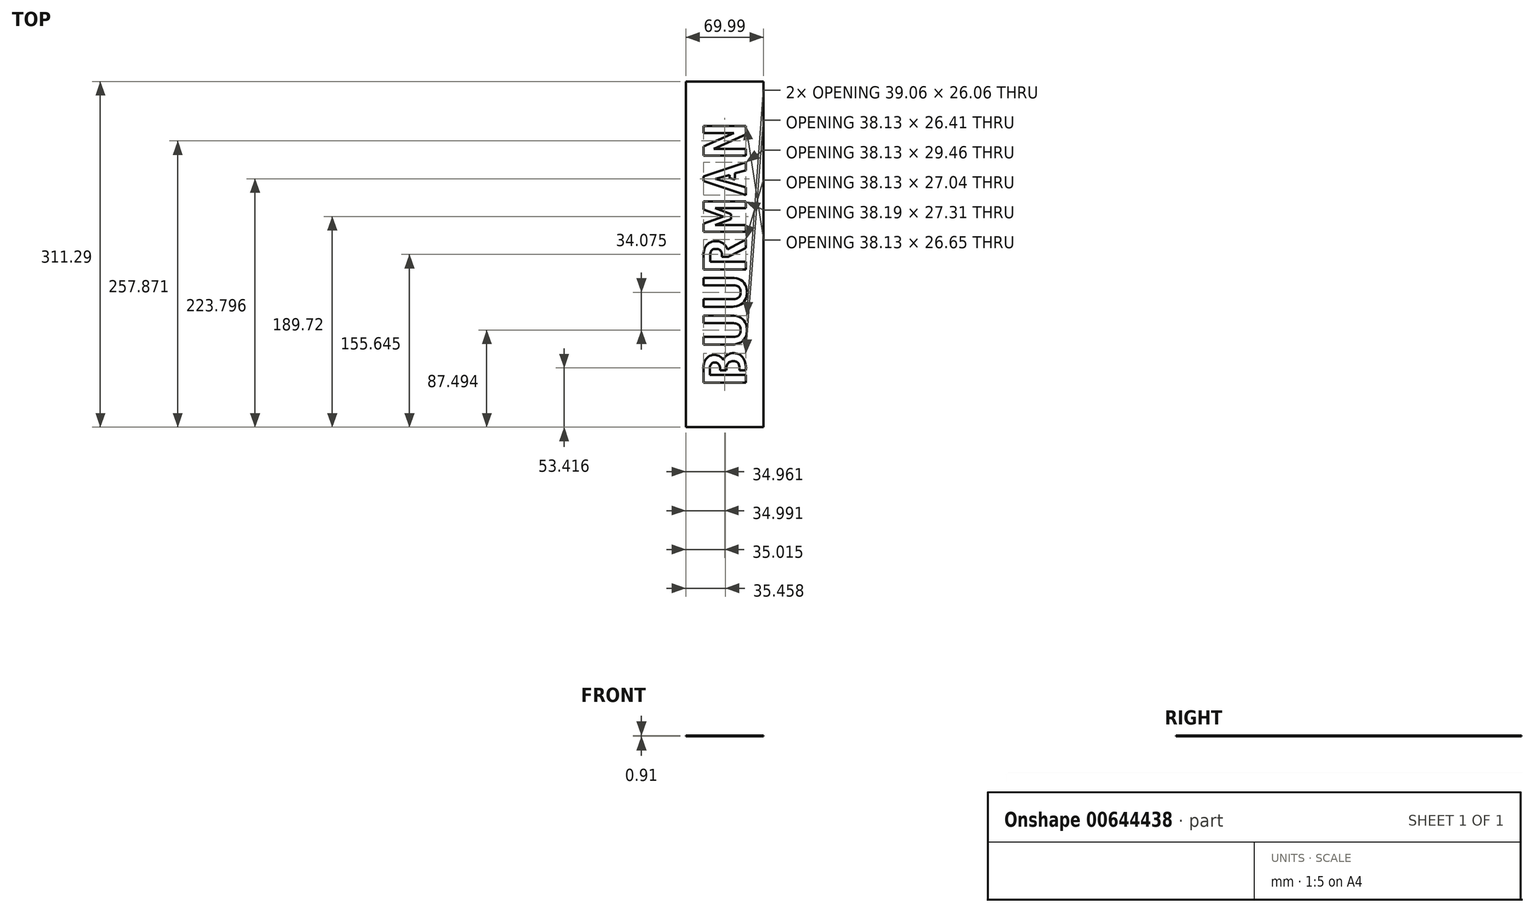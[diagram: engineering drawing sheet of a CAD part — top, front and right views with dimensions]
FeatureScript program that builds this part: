
annotation { "Feature Type Name" : "Feature", "Feature Type Description" : "" }
export const myFeature = defineFeature(function(context is Context, id is Id, definition is map)
    precondition{}
    {
        {
            var Q0;
            Q0=qCreatedBy(makeId("Top.planeOp"),FACE);
            var sketch = newSketch(context, id + "F0", { "sketchPlane" : qUnion([Q0])});
            skLineSegment(sketch, "E0", {"start": v(-753.27, 2930.84) * mm, "end": v(-1506.53, 2930.84) * mm});
            skLineSegment(sketch, "E1", {"start": v(-454.93, 2365.48) * mm, "end": v(-1506.53, 2365.48) * mm});
            skLineSegment(sketch, "E2", {"start": v(-1506.53, 3100.61) * mm, "end": v(-454.93, 3100.61) * mm});
            skLineSegment(sketch, "E3", {"start": v(-1506.53, 2365.48) * mm, "end": v(-1506.53, 2596.24) * mm});
            skLineSegment(sketch, "E4", {"start": v(-454.93, 2535.25) * mm, "end": v(-454.93, 2365.48) * mm});
            skLineSegment(sketch, "E5", {"start": v(-454.93, 2892.1) * mm, "end": v(-1250.22, 2535.25) * mm});
            skLineSegment(sketch, "E6", {"start": v(-1506.53, 2930.84) * mm, "end": v(-1506.53, 3100.61) * mm});
            skLineSegment(sketch, "E7", {"start": v(-454.93, 3100.61) * mm, "end": v(-454.93, 2892.1) * mm});
            skLineSegment(sketch, "E8", {"start": v(-1250.22, 2535.25) * mm, "end": v(-454.93, 2535.25) * mm});
            skLineSegment(sketch, "E9", {"start": v(-1506.53, 2596.24) * mm, "end": v(-753.27, 2930.84) * mm});
            skLineSegment(sketch, "E10", {"start": v(-857.93, 1890.5) * mm, "end": v(-1207.37, 1794.07) * mm});
            skLineSegment(sketch, "E11", {"start": v(-1506.53, 1738.03) * mm, "end": v(-1506.53, 1848.46) * mm});
            skLineSegment(sketch, "E12", {"start": v(-1506.53, 1848.46) * mm, "end": v(-454.93, 2199.55) * mm});
            skLineSegment(sketch, "E13", {"start": v(-454.93, 2199.55) * mm, "end": v(-454.93, 2001.75) * mm});
            skLineSegment(sketch, "E14", {"start": v(-454.93, 1581.44) * mm, "end": v(-454.93, 1386.95) * mm});
            skLineSegment(sketch, "E15", {"start": v(-454.93, 2001.75) * mm, "end": v(-726.9, 1926.76) * mm});
            skLineSegment(sketch, "E16", {"start": v(-726.9, 1926.76) * mm, "end": v(-726.9, 1773.47) * mm});
            skLineSegment(sketch, "E17", {"start": v(-1208.4, 1793.78) * mm, "end": v(-454.93, 1581.44) * mm});
            skLineSegment(sketch, "E18", {"start": v(-454.93, 1386.95) * mm, "end": v(-1506.53, 1738.03) * mm});
            skLineSegment(sketch, "E19", {"start": v(-857.93, 1810.4) * mm, "end": v(-857.93, 1890.5) * mm});
            skLineSegment(sketch, "E20", {"start": v(-1348.44, -2949.46) * mm, "end": v(-1348.44, -3081.32) * mm});
            skLineSegment(sketch, "E21", {"start": v(-1348.44, -3081.32) * mm, "end": v(-454.25, -3081.32) * mm});
            skLineSegment(sketch, "E22", {"start": v(-614.96, -2965.94) * mm, "end": v(-614.96, -2934.62) * mm});
            skLineSegment(sketch, "E23", {"start": v(-454.25, -3081.32) * mm, "end": v(-454.25, -3270.05) * mm});
            skLineSegment(sketch, "E24", {"start": v(-454.25, -3270.05) * mm, "end": v(-1505.85, -3270.05) * mm});
            skLineSegment(sketch, "E25", {"start": v(-1505.85, -3270.05) * mm, "end": v(-1505.85, -2951.1) * mm});
            skLineSegment(sketch, "E26", {"start": v(-829.91, -852.26) * mm, "end": v(-1506.53, -852.26) * mm});
            skLineSegment(sketch, "E27", {"start": v(-1506.53, -852.26) * mm, "end": v(-1506.53, -666.83) * mm});
            skLineSegment(sketch, "E28", {"start": v(-1506.53, -1385.48) * mm, "end": v(-1506.53, -1196.75) * mm});
            skLineSegment(sketch, "E29", {"start": v(-1506.53, -1196.75) * mm, "end": v(-824.97, -1196.75) * mm});
            skLineSegment(sketch, "E30", {"start": v(-826.62, -1385.48) * mm, "end": v(-1506.53, -1385.48) * mm});
            skLineSegment(sketch, "E31", {"start": v(-1506.53, -666.83) * mm, "end": v(-831.56, -666.83) * mm});
            skLineSegment(sketch, "E32", {"start": v(-1506.53, -1606.63) * mm, "end": v(-831.56, -1606.63) * mm});
            skLineSegment(sketch, "E33", {"start": v(-1506.53, -2136.55) * mm, "end": v(-824.97, -2136.55) * mm});
            skLineSegment(sketch, "E34", {"start": v(-826.62, -2325.28) * mm, "end": v(-1506.53, -2325.28) * mm});
            skLineSegment(sketch, "E35", {"start": v(-1506.53, -2325.28) * mm, "end": v(-1506.53, -2136.55) * mm});
            skLineSegment(sketch, "E36", {"start": v(-829.91, -1792.06) * mm, "end": v(-1506.53, -1792.06) * mm});
            skLineSegment(sketch, "E37", {"start": v(-1506.53, -1792.06) * mm, "end": v(-1506.53, -1606.63) * mm});
            skLineSegment(sketch, "E38", {"start": v(-1506.53, 476.81) * mm, "end": v(-1506.53, 676.26) * mm});
            skLineSegment(sketch, "E39", {"start": v(-454.93, 476.81) * mm, "end": v(-1506.53, 476.81) * mm});
            skLineSegment(sketch, "E40", {"start": v(-454.93, 1059.48) * mm, "end": v(-1218.08, 1059.48) * mm});
            skLineSegment(sketch, "E41", {"start": v(-1218.08, 1059.48) * mm, "end": v(-820.85, 912.78) * mm});
            skLineSegment(sketch, "E42", {"start": v(-820.85, 912.78) * mm, "end": v(-820.85, 787.51) * mm});
            skLineSegment(sketch, "E43", {"start": v(-1218.08, 645.76) * mm, "end": v(-454.93, 645.76) * mm});
            skLineSegment(sketch, "E44", {"start": v(-454.93, 645.76) * mm, "end": v(-454.93, 476.81) * mm});
            skLineSegment(sketch, "E45", {"start": v(-820.85, 787.51) * mm, "end": v(-1218.08, 645.76) * mm});
            skLineSegment(sketch, "E46", {"start": v(-1506.53, 676.26) * mm, "end": v(-1012.05, 853.45) * mm});
            skLineSegment(sketch, "E47", {"start": v(-1012.05, 853.45) * mm, "end": v(-1508.18, 1028.99) * mm});
            skLineSegment(sketch, "E48", {"start": v(-1508.18, 1028.99) * mm, "end": v(-1508.18, 1230.08) * mm});
            skLineSegment(sketch, "E49", {"start": v(-1508.18, 1230.08) * mm, "end": v(-454.93, 1230.08) * mm});
            skLineSegment(sketch, "E50", {"start": v(-454.93, 1230.08) * mm, "end": v(-454.93, 1059.48) * mm});
            skLineSegment(sketch, "E51", {"start": v(-1506.53, -459.28) * mm, "end": v(-1506.53, -126.32) * mm});
            skLineSegment(sketch, "E52", {"start": v(-454.93, 286.57) * mm, "end": v(-454.93, 73.94) * mm});
            skLineSegment(sketch, "E53", {"start": v(-912.33, 40.15) * mm, "end": v(-454.93, 286.57) * mm});
            skLineSegment(sketch, "E54", {"start": v(-454.93, 73.94) * mm, "end": v(-890.07, -143.63) * mm});
            skLineSegment(sketch, "E55", {"start": v(-1339.23, -266.43) * mm, "end": v(-454.93, -266.43) * mm});
            skLineSegment(sketch, "E56", {"start": v(-454.93, -266.43) * mm, "end": v(-454.93, -459.28) * mm});
            skLineSegment(sketch, "E57", {"start": v(-1050.78, -143.63) * mm, "end": v(-1050.78, -114.79) * mm});
            skLineSegment(sketch, "E58", {"start": v(-1339.23, -114.79) * mm, "end": v(-1339.23, -266.43) * mm});
            skLineSegment(sketch, "E59", {"start": v(-454.93, -459.28) * mm, "end": v(-1506.53, -459.28) * mm});
            skFitSpline(sketch, "E60", {"points": [v(-1505.85, -2951.1) * mm, v(-1503.48, -2896.62) * mm, v(-1500.12, -2819.58) * mm, v(-1467.8, -2727.6) * mm, v(-1435.59, -2674.72) * mm, v(-1395, -2633.67) * mm, v(-1347.26, -2604.12) * mm, v(-1292.6, -2587) * mm, v(-1232.83, -2581.22) * mm, v(-1169.39, -2589.48) * mm, v(-1109, -2616.14) * mm, v(-1054.43, -2655.71) * mm, v(-1030.03, -2692.88) * mm, v(-1017.96, -2711.28) * mm]});
            skFitSpline(sketch, "E61", {"points": [v(-1017.96, -2711.28) * mm, v(-998.63, -2680.55) * mm, v(-959.8, -2618.83) * mm, v(-867.71, -2559.04) * mm, v(-774.7, -2538.13) * mm, v(-696.27, -2546.32) * mm, v(-634, -2565.32) * mm, v(-579.68, -2598.47) * mm, v(-533.73, -2644.51) * mm, v(-497.24, -2703.7) * mm, v(-471.97, -2775.8) * mm, v(-455.93, -2864.54) * mm, v(-454.86, -2929.39) * mm, v(-454.25, -2965.94) * mm]});
            skFitSpline(sketch, "E62", {"points": [v(-942.14, -2965.94) * mm, v(-940.98, -2930.74) * mm, v(-938.96, -2869.63) * mm, v(-901.55, -2791.6) * mm, v(-840, -2747.52) * mm, v(-768.48, -2736.85) * mm, v(-698.63, -2745.12) * mm, v(-643.77, -2788.35) * mm, v(-618.55, -2856.44) * mm, v(-616.24, -2906.61) * mm, v(-614.96, -2934.62) * mm]});
            skFitSpline(sketch, "E63", {"points": [v(-1348.44, -2949.46) * mm, v(-1346.26, -2916.2) * mm, v(-1342.43, -2857.88) * mm, v(-1293.4, -2788.35) * mm, v(-1227.62, -2769) * mm, v(-1169.26, -2780.88) * mm, v(-1123.55, -2819.55) * mm, v(-1098.16, -2885.62) * mm, v(-1096.43, -2936.6) * mm, v(-1095.43, -2965.94) * mm]});
            skFitSpline(sketch, "E64", {"points": [v(-824.97, -2136.55) * mm, v(-790.76, -2135.1) * mm, v(-730.02, -2132.55) * mm, v(-648.06, -2105.71) * mm, v(-594.62, -2044.75) * mm, v(-585.1, -1965.28) * mm, v(-594.6, -1885.44) * mm, v(-648.85, -1823.05) * mm, v(-732.73, -1796.08) * mm, v(-794.83, -1793.51) * mm, v(-829.91, -1792.06) * mm]});
            skFitSpline(sketch, "E65", {"points": [v(-826.62, -2325.28) * mm, v(-797.07, -2324.3) * mm, v(-740.86, -2322.45) * mm, v(-661.6, -2305.13) * mm, v(-592.4, -2276.43) * mm, v(-533.9, -2235.75) * mm, v(-487.12, -2183.7) * mm, v(-453.97, -2120.47) * mm, v(-434.69, -2047.19) * mm, v(-429.13, -1968.13) * mm, v(-434.61, -1889.34) * mm, v(-453.25, -1816.8) * mm, v(-485.22, -1753.44) * mm, v(-530.1, -1699.8) * mm, v(-588, -1657.08) * mm, v(-658.7, -1627.37) * mm, v(-741.26, -1609.5) * mm, v(-800.28, -1607.62) * mm, v(-831.56, -1606.63) * mm]});
            skFitSpline(sketch, "E66", {"points": [v(-824.97, -1196.75) * mm, v(-790.76, -1195.3) * mm, v(-730.02, -1192.75) * mm, v(-648.06, -1165.91) * mm, v(-594.62, -1104.95) * mm, v(-585.1, -1025.48) * mm, v(-594.6, -945.64) * mm, v(-648.85, -883.25) * mm, v(-732.73, -856.28) * mm, v(-794.83, -853.71) * mm, v(-829.91, -852.26) * mm]});
            skFitSpline(sketch, "E67", {"points": [v(-826.62, -1385.48) * mm, v(-797.07, -1384.5) * mm, v(-740.86, -1382.65) * mm, v(-661.6, -1365.33) * mm, v(-592.4, -1336.63) * mm, v(-533.9, -1295.95) * mm, v(-487.12, -1243.9) * mm, v(-453.97, -1180.67) * mm, v(-434.69, -1107.39) * mm, v(-429.13, -1028.33) * mm, v(-434.61, -949.54) * mm, v(-453.25, -877) * mm, v(-485.22, -813.64) * mm, v(-530.1, -760) * mm, v(-588, -717.28) * mm, v(-658.7, -687.57) * mm, v(-741.26, -669.7) * mm, v(-800.28, -667.82) * mm, v(-831.56, -666.83) * mm]});
            skFitSpline(sketch, "E68", {"points": [v(-1339.23, -114.79) * mm, v(-1338.12, -90.2) * mm, v(-1336.13, -46.45) * mm, v(-1307.65, 11.42) * mm, v(-1254.87, 43.27) * mm, v(-1194.45, 50.15) * mm, v(-1134, 42.36) * mm, v(-1084.26, 9.43) * mm, v(-1054.21, -46.95) * mm, v(-1052, -90.63) * mm, v(-1050.78, -114.79) * mm]});
            skFitSpline(sketch, "E69", {"points": [v(-1506.53, -126.32) * mm, v(-1505.68, -96.86) * mm, v(-1504.1, -41.6) * mm, v(-1488.74, 35.3) * mm, v(-1463.23, 100.39) * mm, v(-1426.14, 152.94) * mm, v(-1379.35, 192.97) * mm, v(-1324.2, 221.52) * mm, v(-1260.88, 237.89) * mm, v(-1196.63, 243.26) * mm, v(-1133.5, 236.96) * mm, v(-1075.94, 217.61) * mm, v(-1021.55, 187.5) * mm, v(-974.14, 146.75) * mm, v(-934.94, 97.76) * mm, v(-919.84, 59.29) * mm, v(-912.33, 40.15) * mm]});
            skLineSegment(sketch, "E70", {"start": v(-1095.43, -2965.94) * mm, "end": v(-942.14, -2965.94) * mm});
            skLineSegment(sketch, "E71", {"start": v(-614.96, -2965.94) * mm, "end": v(-454.25, -2965.94) * mm});
            skLineSegment(sketch, "E72", {"start": v(-1050.78, -143.63) * mm, "end": v(-890.07, -143.63) * mm});
            skLineSegment(sketch, "E73", {"start": v(-726.9, 1773.47) * mm, "end": v(-857.93, 1810.4) * mm});
            skLineSegment(sketch, "E74", {"start": v(-15.5, -4378.95) * mm, "end": v(-1945.9, -4378.95) * mm});
            skLineSegment(sketch, "E75", {"start": v(-15.5, 4206.25) * mm, "end": v(-1945.9, 4206.25) * mm});
            skLineSegment(sketch, "E76", {"start": v(-15.5, -4378.95) * mm, "end": v(-15.5, 4206.25) * mm});
            skLineSegment(sketch, "E77", {"start": v(-1945.9, 4206.25) * mm, "end": v(-1945.9, -4378.95) * mm});
            skLineSegment(sketch, "E78", {"start": v(-1506.53, 1738.03) * mm, "end": v(-454.93, 1386.95) * mm});
            skLineSegment(sketch, "E79", {"start": v(-454.93, 1386.95) * mm, "end": v(-454.93, 1581.44) * mm});
            skLineSegment(sketch, "E80", {"start": v(-454.93, 1581.44) * mm, "end": v(-1207.37, 1794.07) * mm});
            skLineSegment(sketch, "E81", {"start": v(-1207.37, 1794.07) * mm, "end": v(-857.93, 1890.5) * mm});
            skLineSegment(sketch, "E82", {"start": v(-857.93, 1890.5) * mm, "end": v(-857.93, 1810.4) * mm});
            skLineSegment(sketch, "E83", {"start": v(-857.93, 1810.4) * mm, "end": v(-726.9, 1773.47) * mm});
            skLineSegment(sketch, "E84", {"start": v(-726.9, 1773.47) * mm, "end": v(-726.9, 1926.76) * mm});
            skLineSegment(sketch, "E85", {"start": v(-726.9, 1926.76) * mm, "end": v(-454.93, 2001.75) * mm});
            skLineSegment(sketch, "E86", {"start": v(-454.93, 2001.75) * mm, "end": v(-454.93, 2199.55) * mm});
            skLineSegment(sketch, "E87", {"start": v(-454.93, 2199.55) * mm, "end": v(-1506.53, 1848.46) * mm});
            skLineSegment(sketch, "E88", {"start": v(-1506.53, 1848.46) * mm, "end": v(-1506.53, 1738.03) * mm});
            skSolve(sketch);
        }
        {
            var Q0;
            Q0 = qSketchRegion(id + "F0", true);
            extrude(context, id + "F1", {"entities" : qUnion([Q0]), "depth" : 25 * mm, "offsetDistance" : 25 * mm});
        }
        {
            var Q0;
            Q0=makeQuery(id+"F1.opExtrude","SWEPT_BODY",BODY,{"disambiguationData":[OSD([sQuery(id+"F0.wireOp",EDGE,"E0"),sQuery(id+"F0.wireOp",EDGE,"E1"),sQuery(id+"F0.wireOp",EDGE,"E2"),sQuery(id+"F0.wireOp",EDGE,"E3"),sQuery(id+"F0.wireOp",EDGE,"E4"),sQuery(id+"F0.wireOp",EDGE,"E5"),sQuery(id+"F0.wireOp",EDGE,"E6"),sQuery(id+"F0.wireOp",EDGE,"E7"),sQuery(id+"F0.wireOp",EDGE,"E8"),sQuery(id+"F0.wireOp",EDGE,"E9"),sQuery(id+"F0.wireOp",EDGE,"E20"),sQuery(id+"F0.wireOp",EDGE,"E21"),sQuery(id+"F0.wireOp",EDGE,"E22"),sQuery(id+"F0.wireOp",EDGE,"E23"),sQuery(id+"F0.wireOp",EDGE,"E24"),sQuery(id+"F0.wireOp",EDGE,"E25"),sQuery(id+"F0.wireOp",EDGE,"E26"),sQuery(id+"F0.wireOp",EDGE,"E27"),sQuery(id+"F0.wireOp",EDGE,"E28"),sQuery(id+"F0.wireOp",EDGE,"E29"),sQuery(id+"F0.wireOp",EDGE,"E30"),sQuery(id+"F0.wireOp",EDGE,"E31"),sQuery(id+"F0.wireOp",EDGE,"E32"),sQuery(id+"F0.wireOp",EDGE,"E33"),sQuery(id+"F0.wireOp",EDGE,"E34"),sQuery(id+"F0.wireOp",EDGE,"E35"),sQuery(id+"F0.wireOp",EDGE,"E36"),sQuery(id+"F0.wireOp",EDGE,"E37"),sQuery(id+"F0.wireOp",EDGE,"E38"),sQuery(id+"F0.wireOp",EDGE,"E39"),sQuery(id+"F0.wireOp",EDGE,"E40"),sQuery(id+"F0.wireOp",EDGE,"E41"),sQuery(id+"F0.wireOp",EDGE,"E42"),sQuery(id+"F0.wireOp",EDGE,"E43"),sQuery(id+"F0.wireOp",EDGE,"E44"),sQuery(id+"F0.wireOp",EDGE,"E45"),sQuery(id+"F0.wireOp",EDGE,"E46"),sQuery(id+"F0.wireOp",EDGE,"E47"),sQuery(id+"F0.wireOp",EDGE,"E48"),sQuery(id+"F0.wireOp",EDGE,"E49"),sQuery(id+"F0.wireOp",EDGE,"E50"),sQuery(id+"F0.wireOp",EDGE,"E51"),sQuery(id+"F0.wireOp",EDGE,"E52"),sQuery(id+"F0.wireOp",EDGE,"E53"),sQuery(id+"F0.wireOp",EDGE,"E54"),sQuery(id+"F0.wireOp",EDGE,"E55"),sQuery(id+"F0.wireOp",EDGE,"E56"),sQuery(id+"F0.wireOp",EDGE,"E57"),sQuery(id+"F0.wireOp",EDGE,"E58"),sQuery(id+"F0.wireOp",EDGE,"E59"),sQuery(id+"F0.wireOp",EDGE,"E60"),sQuery(id+"F0.wireOp",EDGE,"E61"),sQuery(id+"F0.wireOp",EDGE,"E62"),sQuery(id+"F0.wireOp",EDGE,"E63"),sQuery(id+"F0.wireOp",EDGE,"E64"),sQuery(id+"F0.wireOp",EDGE,"E65"),sQuery(id+"F0.wireOp",EDGE,"E66"),sQuery(id+"F0.wireOp",EDGE,"E67"),sQuery(id+"F0.wireOp",EDGE,"E68"),sQuery(id+"F0.wireOp",EDGE,"E69"),sQuery(id+"F0.wireOp",EDGE,"E70"),sQuery(id+"F0.wireOp",EDGE,"E71"),sQuery(id+"F0.wireOp",EDGE,"E72"),sQuery(id+"F0.wireOp",EDGE,"E74"),sQuery(id+"F0.wireOp",EDGE,"E75"),sQuery(id+"F0.wireOp",EDGE,"E76"),sQuery(id+"F0.wireOp",EDGE,"E77"),sQuery(id+"F0.wireOp",EDGE,"E78"),sQuery(id+"F0.wireOp",EDGE,"E79"),sQuery(id+"F0.wireOp",EDGE,"E80"),sQuery(id+"F0.wireOp",EDGE,"E81"),sQuery(id+"F0.wireOp",EDGE,"E82"),sQuery(id+"F0.wireOp",EDGE,"E83"),sQuery(id+"F0.wireOp",EDGE,"E84"),sQuery(id+"F0.wireOp",EDGE,"E85"),sQuery(id+"F0.wireOp",EDGE,"E86"),sQuery(id+"F0.wireOp",EDGE,"E87"),sQuery(id+"F0.wireOp",EDGE,"E88")])]});
            var Q1;
            Q1=makeQuery(id+"F1.opExtrude","CAP_VERTEX",VERTEX,{"disambiguationData":[OSD([sQuery(id+"F0.wireOp",EDGE,"E23"),sQuery(id+"F0.wireOp",EDGE,"E24")])],"isStart":false});
            transform(context, id + "F2", {"entities" : qUnion([Q0]), "transformType" : TransformType.SCALE_UNIFORMLY, "scale" : 1 / 27.58, "scalePoint" : qUnion([Q1]), "makeCopy" : false});
        }
        {
            var Q0;
            Q0=qCreatedBy(makeId("Top.planeOp"),FACE);
            var sketch = newSketch(context, id + "F3", { "sketchPlane" : qUnion([Q0])});
            skLineSegment(sketch, "E89", {"start": v(-128.42, 679.2) * mm, "end": v(-128.42, 1568.2) * mm});
            skLineSegment(sketch, "E90", {"start": v(-128.42, 1568.2) * mm, "end": v(-382.42, 1568.2) * mm});
            skLineSegment(sketch, "E91", {"start": v(-382.42, 1568.2) * mm, "end": v(-382.42, 1644.4) * mm});
            skLineSegment(sketch, "E92", {"start": v(-382.42, 1644.4) * mm, "end": v(-890.42, 1644.4) * mm});
            skLineSegment(sketch, "E93", {"start": v(-890.42, 1644.4) * mm, "end": v(-890.42, 1568.2) * mm});
            skLineSegment(sketch, "E94", {"start": v(-890.42, 1568.2) * mm, "end": v(-1144.42, 1568.2) * mm});
            skLineSegment(sketch, "E95", {"start": v(-1144.42, 1568.2) * mm, "end": v(-1144.42, 679.2) * mm});
            skLineSegment(sketch, "E96", {"start": v(-1144.42, -5975.6) * mm, "end": v(-890.42, -5975.6) * mm});
            skLineSegment(sketch, "E97", {"start": v(-890.42, -5975.6) * mm, "end": v(-890.42, -5899.4) * mm});
            skLineSegment(sketch, "E98", {"start": v(-890.42, -5899.4) * mm, "end": v(-1144.42, -5899.4) * mm});
            skLineSegment(sketch, "E99", {"start": v(-1144.42, -5899.4) * mm, "end": v(-1144.42, -5035.8) * mm});
            skLineSegment(sketch, "E100", {"start": v(-128.42, -5975.6) * mm, "end": v(-382.42, -5975.6) * mm});
            skLineSegment(sketch, "E101", {"start": v(-382.42, -5975.6) * mm, "end": v(-382.42, -5899.4) * mm});
            skLineSegment(sketch, "E102", {"start": v(-382.42, -5899.4) * mm, "end": v(-128.42, -5899.4) * mm});
            skLineSegment(sketch, "E103", {"start": v(-128.42, -5899.4) * mm, "end": v(-128.42, -5035.8) * mm});
            skLineSegment(sketch, "E104", {"start": v(-1144.42, -5035.8) * mm, "end": v(-890.42, -5035.8) * mm});
            skLineSegment(sketch, "E105", {"start": v(-890.42, -5035.8) * mm, "end": v(-890.42, -4959.6) * mm});
            skLineSegment(sketch, "E106", {"start": v(-890.42, -4959.6) * mm, "end": v(-1144.42, -4959.6) * mm});
            skLineSegment(sketch, "E107", {"start": v(-1144.42, -4959.6) * mm, "end": v(-1144.42, -4096) * mm});
            skLineSegment(sketch, "E108", {"start": v(-128.42, -5035.8) * mm, "end": v(-382.42, -5035.8) * mm});
            skLineSegment(sketch, "E109", {"start": v(-382.42, -5035.8) * mm, "end": v(-382.42, -4959.6) * mm});
            skLineSegment(sketch, "E110", {"start": v(-382.42, -4959.6) * mm, "end": v(-128.42, -4959.6) * mm});
            skLineSegment(sketch, "E111", {"start": v(-128.42, -4959.6) * mm, "end": v(-128.42, -4096) * mm});
            skLineSegment(sketch, "E112", {"start": v(-1144.42, -4096) * mm, "end": v(-890.42, -4096) * mm});
            skLineSegment(sketch, "E113", {"start": v(-890.42, -4096) * mm, "end": v(-890.42, -4019.8) * mm});
            skLineSegment(sketch, "E114", {"start": v(-890.42, -4019.8) * mm, "end": v(-1144.42, -4019.8) * mm});
            skLineSegment(sketch, "E115", {"start": v(-1144.42, -4019.8) * mm, "end": v(-1144.42, -3156.2) * mm});
            skLineSegment(sketch, "E116", {"start": v(-128.42, -4096) * mm, "end": v(-382.42, -4096) * mm});
            skLineSegment(sketch, "E117", {"start": v(-382.42, -4096) * mm, "end": v(-382.42, -4019.8) * mm});
            skLineSegment(sketch, "E118", {"start": v(-382.42, -4019.8) * mm, "end": v(-128.42, -4019.8) * mm});
            skLineSegment(sketch, "E119", {"start": v(-128.42, -4019.8) * mm, "end": v(-128.42, -3156.2) * mm});
            skLineSegment(sketch, "E120", {"start": v(-1144.42, -3156.2) * mm, "end": v(-890.42, -3156.2) * mm});
            skLineSegment(sketch, "E121", {"start": v(-890.42, -3156.2) * mm, "end": v(-890.42, -3080) * mm});
            skLineSegment(sketch, "E122", {"start": v(-890.42, -3080) * mm, "end": v(-1144.42, -3080) * mm});
            skLineSegment(sketch, "E123", {"start": v(-1144.42, -3080) * mm, "end": v(-1144.42, -2216.4) * mm});
            skLineSegment(sketch, "E124", {"start": v(-128.42, -3156.2) * mm, "end": v(-382.42, -3156.2) * mm});
            skLineSegment(sketch, "E125", {"start": v(-382.42, -3156.2) * mm, "end": v(-382.42, -3080) * mm});
            skLineSegment(sketch, "E126", {"start": v(-382.42, -3080) * mm, "end": v(-128.42, -3080) * mm});
            skLineSegment(sketch, "E127", {"start": v(-128.42, -3080) * mm, "end": v(-128.42, -2216.4) * mm});
            skLineSegment(sketch, "E128", {"start": v(-1144.42, -2216.4) * mm, "end": v(-890.42, -2216.4) * mm});
            skLineSegment(sketch, "E129", {"start": v(-890.42, -2216.4) * mm, "end": v(-890.42, -2140.2) * mm});
            skLineSegment(sketch, "E130", {"start": v(-890.42, -2140.2) * mm, "end": v(-1144.42, -2140.2) * mm});
            skLineSegment(sketch, "E131", {"start": v(-1144.42, -2140.2) * mm, "end": v(-1144.42, -1276.6) * mm});
            skLineSegment(sketch, "E132", {"start": v(-128.42, -2216.4) * mm, "end": v(-382.42, -2216.4) * mm});
            skLineSegment(sketch, "E133", {"start": v(-382.42, -2216.4) * mm, "end": v(-382.42, -2140.2) * mm});
            skLineSegment(sketch, "E134", {"start": v(-382.42, -2140.2) * mm, "end": v(-128.42, -2140.2) * mm});
            skLineSegment(sketch, "E135", {"start": v(-128.42, -2140.2) * mm, "end": v(-128.42, -1276.6) * mm});
            skLineSegment(sketch, "E136", {"start": v(-1144.42, -1276.6) * mm, "end": v(-890.42, -1276.6) * mm});
            skLineSegment(sketch, "E137", {"start": v(-890.42, -1276.6) * mm, "end": v(-890.42, -1200.4) * mm});
            skLineSegment(sketch, "E138", {"start": v(-890.42, -1200.4) * mm, "end": v(-1144.42, -1200.4) * mm});
            skLineSegment(sketch, "E139", {"start": v(-1144.42, -1200.4) * mm, "end": v(-1144.42, -336.8) * mm});
            skLineSegment(sketch, "E140", {"start": v(-128.42, -1276.6) * mm, "end": v(-382.42, -1276.6) * mm});
            skLineSegment(sketch, "E141", {"start": v(-382.42, -1276.6) * mm, "end": v(-382.42, -1200.4) * mm});
            skLineSegment(sketch, "E142", {"start": v(-382.42, -1200.4) * mm, "end": v(-128.42, -1200.4) * mm});
            skLineSegment(sketch, "E143", {"start": v(-128.42, -1200.4) * mm, "end": v(-128.42, -336.8) * mm});
            skLineSegment(sketch, "E144", {"start": v(-1144.42, -336.8) * mm, "end": v(-890.42, -336.8) * mm});
            skLineSegment(sketch, "E145", {"start": v(-890.42, -336.8) * mm, "end": v(-890.42, -260.6) * mm});
            skLineSegment(sketch, "E146", {"start": v(-890.42, -260.6) * mm, "end": v(-1144.42, -260.6) * mm});
            skLineSegment(sketch, "E147", {"start": v(-1144.42, -260.6) * mm, "end": v(-1144.42, 603) * mm});
            skLineSegment(sketch, "E148", {"start": v(-128.42, -336.8) * mm, "end": v(-382.42, -336.8) * mm});
            skLineSegment(sketch, "E149", {"start": v(-382.42, -336.8) * mm, "end": v(-382.42, -260.6) * mm});
            skLineSegment(sketch, "E150", {"start": v(-382.42, -260.6) * mm, "end": v(-128.42, -260.6) * mm});
            skLineSegment(sketch, "E151", {"start": v(-128.42, -260.6) * mm, "end": v(-128.42, 603) * mm});
            skLineSegment(sketch, "E152", {"start": v(-1144.42, 603) * mm, "end": v(-890.42, 603) * mm});
            skLineSegment(sketch, "E153", {"start": v(-890.42, 603) * mm, "end": v(-890.42, 679.2) * mm});
            skLineSegment(sketch, "E154", {"start": v(-890.42, 679.2) * mm, "end": v(-1144.42, 679.2) * mm});
            skLineSegment(sketch, "E155", {"start": v(-128.42, 603) * mm, "end": v(-382.42, 603) * mm});
            skLineSegment(sketch, "E156", {"start": v(-382.42, 603) * mm, "end": v(-382.42, 679.2) * mm});
            skLineSegment(sketch, "E157", {"start": v(-382.42, 679.2) * mm, "end": v(-128.42, 679.2) * mm});
            skLineSegment(sketch, "E158", {"start": v(-1144.42, -5975.6) * mm, "end": v(-1144.42, -6864.6) * mm});
            skLineSegment(sketch, "E159", {"start": v(-1144.42, -6864.6) * mm, "end": v(-890.42, -6864.6) * mm});
            skLineSegment(sketch, "E160", {"start": v(-890.42, -6864.6) * mm, "end": v(-890.42, -6940.8) * mm});
            skLineSegment(sketch, "E161", {"start": v(-890.42, -6940.8) * mm, "end": v(-382.42, -6940.8) * mm});
            skLineSegment(sketch, "E162", {"start": v(-382.42, -6940.8) * mm, "end": v(-382.42, -6864.6) * mm});
            skLineSegment(sketch, "E163", {"start": v(-382.42, -6864.6) * mm, "end": v(-128.42, -6864.6) * mm});
            skLineSegment(sketch, "E164", {"start": v(-128.42, -6864.6) * mm, "end": v(-128.42, -5975.6) * mm});
            skSolve(sketch);
        }
        {
            var Q0;
            Q0=sQuery(id+"F3.wireOp",EDGE,"E161");
            var Q1;
            Q1=sQuery(id+"F3.wireOp",EDGE,"E158");
            var Q2;
            Q2=sQuery(id+"F3.wireOp",EDGE,"E151");
            var Q3;
            Q3=sQuery(id+"F3.wireOp",EDGE,"E119");
            var Q4;
            Q4=sQuery(id+"F3.wireOp",EDGE,"E135");
            var Q5;
            Q5=sQuery(id+"F3.wireOp",EDGE,"E111");
            var Q6;
            Q6=sQuery(id+"F3.wireOp",EDGE,"E143");
            var Q7;
            Q7=sQuery(id+"F3.wireOp",EDGE,"E127");
            var Q8;
            Q8=sQuery(id+"F3.wireOp",EDGE,"E103");
            var Q9;
            Q9=sQuery(id+"F3.wireOp",EDGE,"E107");
            var Q10;
            Q10=sQuery(id+"F3.wireOp",EDGE,"E139");
            var Q11;
            Q11=sQuery(id+"F3.wireOp",EDGE,"E123");
            var Q12;
            Q12=sQuery(id+"F3.wireOp",EDGE,"E89");
            var Q13;
            Q13=sQuery(id+"F3.wireOp",EDGE,"E92");
            var Q14;
            Q14=sQuery(id+"F3.wireOp",EDGE,"E95");
            var Q15;
            Q15=sQuery(id+"F3.wireOp",EDGE,"E99");
            var Q16;
            Q16=sQuery(id+"F3.wireOp",EDGE,"E115");
            var Q17;
            Q17=sQuery(id+"F3.wireOp",EDGE,"E131");
            var Q18;
            Q18=sQuery(id+"F3.wireOp",EDGE,"E147");
            var Q19;
            Q19=sQuery(id+"F3.wireOp",EDGE,"E164");
            var Q20;
            Q20=sQuery(id+"F3.wireOp",EDGE,"E160");
            var Q21;
            Q21=sQuery(id+"F3.wireOp",EDGE,"E149");
            var Q22;
            Q22=sQuery(id+"F3.wireOp",EDGE,"E133");
            var Q23;
            Q23=sQuery(id+"F3.wireOp",EDGE,"E117");
            var Q24;
            Q24=sQuery(id+"F3.wireOp",EDGE,"E145");
            var Q25;
            Q25=sQuery(id+"F3.wireOp",EDGE,"E129");
            var Q26;
            Q26=sQuery(id+"F3.wireOp",EDGE,"E113");
            var Q27;
            Q27=sQuery(id+"F3.wireOp",EDGE,"E110");
            var Q28;
            Q28=sQuery(id+"F3.wireOp",EDGE,"E142");
            var Q29;
            Q29=sQuery(id+"F3.wireOp",EDGE,"E126");
            var Q30;
            Q30=sQuery(id+"F3.wireOp",EDGE,"E106");
            var Q31;
            Q31=sQuery(id+"F3.wireOp",EDGE,"E154");
            var Q32;
            Q32=sQuery(id+"F3.wireOp",EDGE,"E138");
            var Q33;
            Q33=sQuery(id+"F3.wireOp",EDGE,"E122");
            var Q34;
            Q34=sQuery(id+"F3.wireOp",EDGE,"E130");
            var Q35;
            Q35=sQuery(id+"F3.wireOp",EDGE,"E146");
            var Q36;
            Q36=sQuery(id+"F3.wireOp",EDGE,"E114");
            var Q37;
            Q37=sQuery(id+"F3.wireOp",EDGE,"E162");
            var Q38;
            Q38=sQuery(id+"F3.wireOp",EDGE,"E152");
            var Q39;
            Q39=sQuery(id+"F3.wireOp",EDGE,"E159");
            var Q40;
            Q40=sQuery(id+"F3.wireOp",EDGE,"E136");
            var Q41;
            Q41=sQuery(id+"F3.wireOp",EDGE,"E120");
            var Q42;
            Q42=sQuery(id+"F3.wireOp",EDGE,"E102");
            var Q43;
            Q43=sQuery(id+"F3.wireOp",EDGE,"E104");
            var Q44;
            Q44=sQuery(id+"F3.wireOp",EDGE,"E155");
            var Q45;
            Q45=sQuery(id+"F3.wireOp",EDGE,"E90");
            var Q46;
            Q46=sQuery(id+"F3.wireOp",EDGE,"E91");
            var Q47;
            Q47=sQuery(id+"F3.wireOp",EDGE,"E93");
            var Q48;
            Q48=sQuery(id+"F3.wireOp",EDGE,"E94");
            var Q49;
            Q49=sQuery(id+"F3.wireOp",EDGE,"E96");
            var Q50;
            Q50=sQuery(id+"F3.wireOp",EDGE,"E97");
            var Q51;
            Q51=sQuery(id+"F3.wireOp",EDGE,"E98");
            var Q52;
            Q52=sQuery(id+"F3.wireOp",EDGE,"E100");
            var Q53;
            Q53=sQuery(id+"F3.wireOp",EDGE,"E101");
            var Q54;
            Q54=sQuery(id+"F3.wireOp",EDGE,"E163");
            var Q55;
            Q55=sQuery(id+"F3.wireOp",EDGE,"E108");
            var Q56;
            Q56=sQuery(id+"F3.wireOp",EDGE,"E156");
            var Q57;
            Q57=sQuery(id+"F3.wireOp",EDGE,"E140");
            var Q58;
            Q58=sQuery(id+"F3.wireOp",EDGE,"E124");
            var Q59;
            Q59=sQuery(id+"F3.wireOp",EDGE,"E153");
            var Q60;
            Q60=sQuery(id+"F3.wireOp",EDGE,"E137");
            var Q61;
            Q61=sQuery(id+"F3.wireOp",EDGE,"E121");
            var Q62;
            Q62=sQuery(id+"F3.wireOp",EDGE,"E148");
            var Q63;
            Q63=sQuery(id+"F3.wireOp",EDGE,"E132");
            var Q64;
            Q64=sQuery(id+"F3.wireOp",EDGE,"E116");
            var Q65;
            Q65=sQuery(id+"F3.wireOp",EDGE,"E144");
            var Q66;
            Q66=sQuery(id+"F3.wireOp",EDGE,"E128");
            var Q67;
            Q67=sQuery(id+"F3.wireOp",EDGE,"E112");
            var Q68;
            Q68=sQuery(id+"F3.wireOp",EDGE,"E109");
            var Q69;
            Q69=sQuery(id+"F3.wireOp",EDGE,"E150");
            var Q70;
            Q70=sQuery(id+"F3.wireOp",EDGE,"E141");
            var Q71;
            Q71=sQuery(id+"F3.wireOp",EDGE,"E157");
            var Q72;
            Q72=sQuery(id+"F3.wireOp",EDGE,"E118");
            var Q73;
            Q73=sQuery(id+"F3.wireOp",EDGE,"E134");
            var Q74;
            Q74=sQuery(id+"F3.wireOp",EDGE,"E125");
            var Q75;
            Q75=sQuery(id+"F3.wireOp",EDGE,"E105");
            extrude(context, id + "F4", {"bodyType" : ToolBodyType.SURFACE, "surfaceEntities" : qUnion([Q0, Q1, Q2, Q3, Q4, Q5, Q6, Q7, Q8, Q9, Q10, Q11, Q12, Q13, Q14, Q15, Q16, Q17, Q18, Q19, Q20, Q21, Q22, Q23, Q24, Q25, Q26, Q27, Q28, Q29, Q30, Q31, Q32, Q33, Q34, Q35, Q36, Q37, Q38, Q39, Q40, Q41, Q42, Q43, Q44, Q45, Q46, Q47, Q48, Q49, Q50, Q51, Q52, Q53, Q54, Q55, Q56, Q57, Q58, Q59, Q60, Q61, Q62, Q63, Q64, Q65, Q66, Q67, Q68, Q69, Q70, Q71, Q72, Q73, Q74, Q75]), "depth" : 1000 * mm, "offsetDistance" : 25 * mm});
        }
    });
